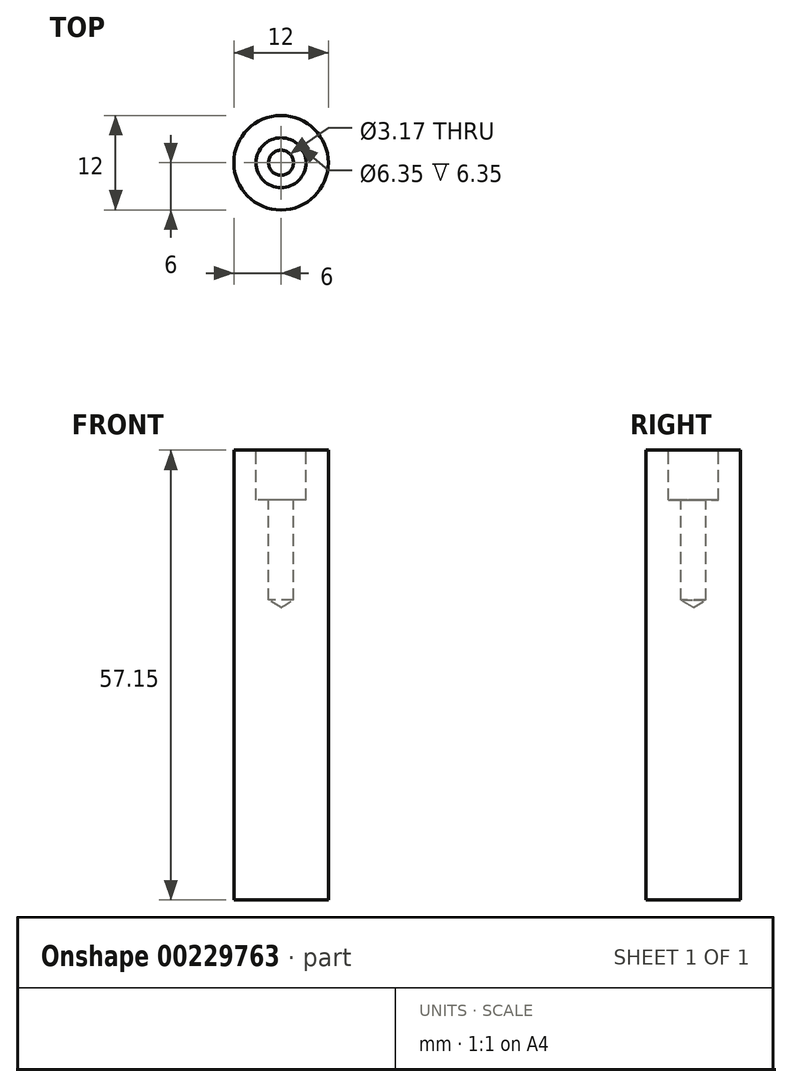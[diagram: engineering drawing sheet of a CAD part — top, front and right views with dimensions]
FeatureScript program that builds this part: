
annotation { "Feature Type Name" : "Feature", "Feature Type Description" : "" }
export const myFeature = defineFeature(function(context is Context, id is Id, definition is map)
    precondition{}
    {
        {
            var Q0;
            Q0=qCreatedBy(makeId("Top.planeOp"),FACE);
            var sketch = newSketch(context, id + "F0", { "sketchPlane" : qUnion([Q0])});
            skCircle(sketch, "E0", {"center": v(0, 0) * mm, "radius": 6 * mm});
            skSolve(sketch);
        }
        {
            var Q0;
            Q0=makeQuery(id+"F0.imprint","IMPRINT",FACE,{"disambiguationData":[TD([[makeQuery(id+"F0.imprint","IMPRINT",EDGE,{"derivedFrom":sQuery(id+"F0.wireOp",EDGE,"E0")}),1.0]])]});
            extrude(context, id + "F1", {"entities" : qUnion([Q0]), "depth" : 57.15 * mm});
        }
        {
            var Q0;
            Q0=makeQuery(id+"F1.opExtrude","CAP_FACE",FACE,{"disambiguationData":[OSD([sQuery(id+"F0.wireOp",EDGE,"E0")])],"isStart":false});
            var sketch = newSketch(context, id + "F2", { "sketchPlane" : qUnion([Q0])});
            skPoint(sketch, "E1", {"position": v(0, 0) * mm});
            skSolve(sketch);
        }
        {
            var Q0;
            Q0=sQuery(id+"F2.wireOp",VERTEX,"E1");
            var Q1;
            Q1=makeQuery(id+"F1.opExtrude","SWEPT_BODY",BODY,{"disambiguationData":[OSD([sQuery(id+"F0.wireOp",EDGE,"E0")])]});
            hole(context, id + "F3", {"style" : HoleStyle.C_BORE, "endStyle" : HoleEndStyle.BLIND, "holeDiameter" : 3.17 * mm, "cBoreDiameter" : 6.35 * mm, "cBoreDepth" : 6.35 * mm, "holeDepth" : 19.05 * mm, "locations" : qUnion([Q0]), "scope" : qUnion([Q1])});
        }
    });
